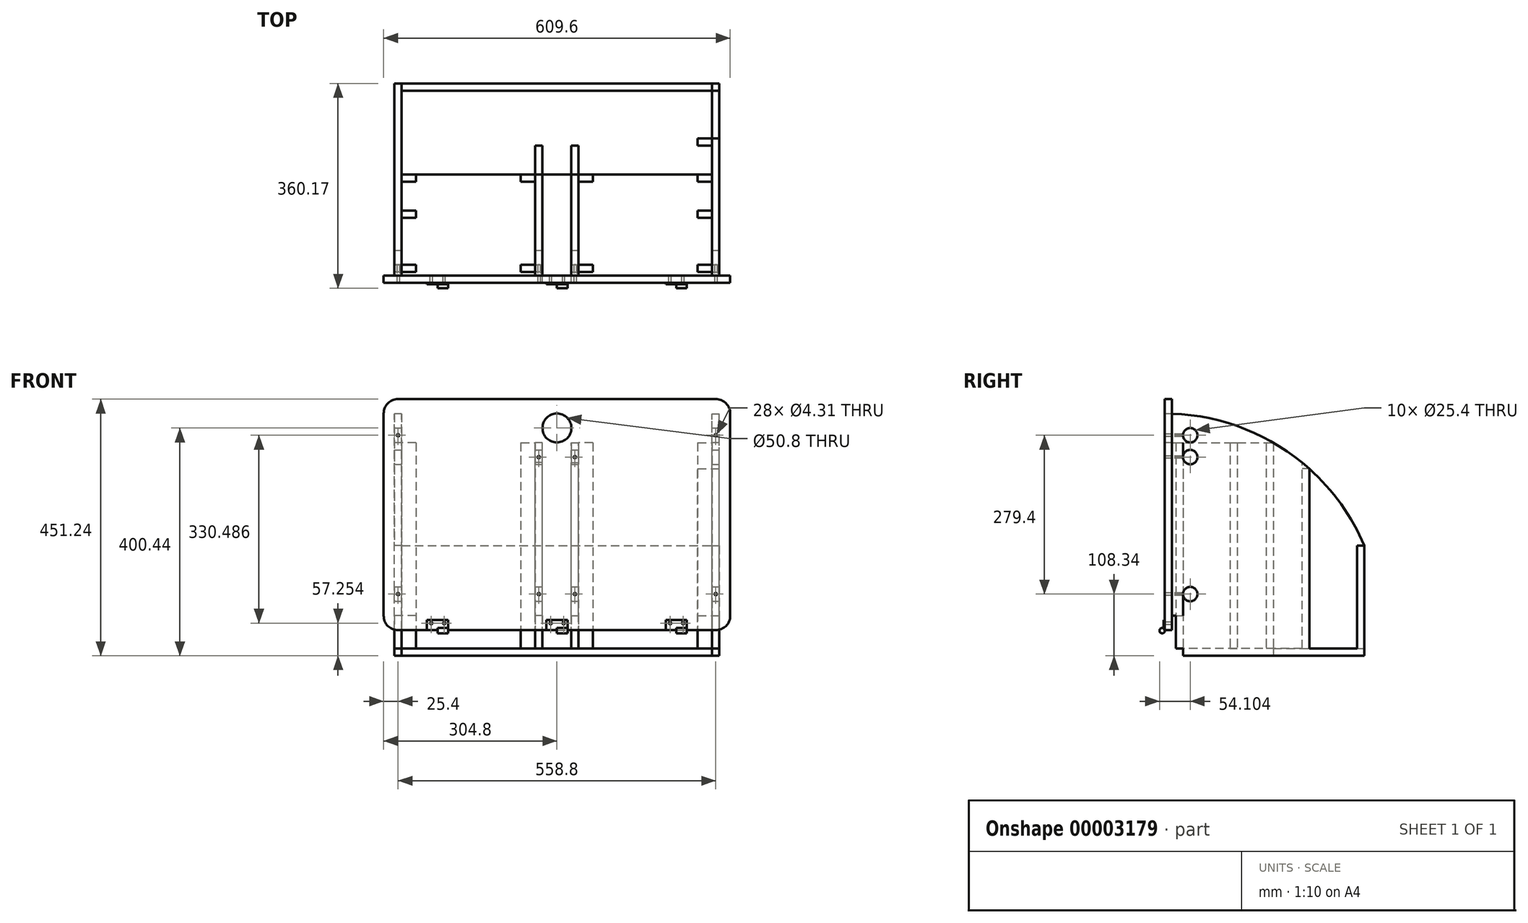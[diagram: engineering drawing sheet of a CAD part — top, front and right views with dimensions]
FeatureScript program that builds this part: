
annotation { "Feature Type Name" : "Feature", "Feature Type Description" : "" }
export const myFeature = defineFeature(function(context is Context, id is Id, definition is map)
    precondition{}
    {
        {
            var Q0;
            Q0=qCreatedBy(makeId("Front.planeOp"),FACE);
            var sketch = newSketch(context, id + "F0", { "sketchPlane" : qUnion([Q0])});
            skLineSegment(sketch, "E0.bottom", {"start": v(25.4, 0) * mm, "end": v(584.2, 0) * mm});
            skLineSegment(sketch, "E0.top", {"start": v(25.4, 406.4) * mm, "end": v(584.2, 406.4) * mm});
            skLineSegment(sketch, "E0.left", {"start": v(0, 25.4) * mm, "end": v(0, 381) * mm});
            skLineSegment(sketch, "E0.right", {"start": v(609.6, 25.4) * mm, "end": v(609.6, 381) * mm});
            skPoint(sketch, "E1.visualSharp", {"position": v(0, 406.4) * mm});
            skArc(sketch, "E1.filletArc", {"start": v(25.4, 406.4) * mm, "mid": v(7.44, 398.96) * mm, "end": v(0, 381) * mm});
            skPoint(sketch, "E2.visualSharp", {"position": v(609.6, 406.4) * mm});
            skArc(sketch, "E2.filletArc", {"start": v(609.6, 381) * mm, "mid": v(602.16, 398.96) * mm, "end": v(584.2, 406.4) * mm});
            skPoint(sketch, "E3.visualSharp", {"position": v(609.6, 0) * mm});
            skArc(sketch, "E3.filletArc", {"start": v(584.2, 0) * mm, "mid": v(602.16, 7.44) * mm, "end": v(609.6, 25.4) * mm});
            skPoint(sketch, "E4.visualSharp", {"position": v(0, 0) * mm});
            skArc(sketch, "E4.filletArc", {"start": v(0, 25.4) * mm, "mid": v(7.44, 7.44) * mm, "end": v(25.4, 0) * mm});
            skCircle(sketch, "E5", {"center": v(304.8, 355.6) * mm, "radius": 25.4 * mm});
            skLineSegment(sketch, "E6.top", {"start": v(76.2, 18.26) * mm, "end": v(113.28, 18.26) * mm});
            skLineSegment(sketch, "E6.left", {"start": v(76.2, -0.8) * mm, "end": v(76.2, 18.26) * mm});
            skLineSegment(sketch, "E6.right", {"start": v(113.28, -0.8) * mm, "end": v(113.28, 18.26) * mm});
            skCircle(sketch, "E7", {"center": v(83.7, 12.41) * mm, "radius": 2.15 * mm});
            skCircle(sketch, "E8", {"center": v(106.55, 12.41) * mm, "radius": 2.15 * mm});
            skLineSegment(sketch, "E9", {"start": v(76.2, -0.8) * mm, "end": v(113.28, -0.8) * mm});
            skLineSegment(sketch, "E10.bottom", {"start": v(286.26, 18.26) * mm, "end": v(323.34, 18.26) * mm});
            skLineSegment(sketch, "E10.top", {"start": v(286.26, -0.8) * mm, "end": v(323.34, -0.8) * mm});
            skLineSegment(sketch, "E10.left", {"start": v(286.26, 18.26) * mm, "end": v(286.26, -0.8) * mm});
            skLineSegment(sketch, "E10.right", {"start": v(323.34, 18.26) * mm, "end": v(323.34, -0.8) * mm});
            skLineSegment(sketch, "E11.bottom", {"start": v(496.32, 18.26) * mm, "end": v(533.4, 18.26) * mm});
            skLineSegment(sketch, "E11.top", {"start": v(496.32, -0.8) * mm, "end": v(533.4, -0.8) * mm});
            skLineSegment(sketch, "E11.left", {"start": v(496.32, 18.26) * mm, "end": v(496.32, -0.8) * mm});
            skLineSegment(sketch, "E11.right", {"start": v(533.4, 18.26) * mm, "end": v(533.4, -0.8) * mm});
            skCircle(sketch, "E12", {"center": v(293.75, 12.41) * mm, "radius": 2.15 * mm});
            skCircle(sketch, "E13", {"center": v(316.61, 12.41) * mm, "radius": 2.15 * mm});
            skCircle(sketch, "E14", {"center": v(503.8, 12.41) * mm, "radius": 2.15 * mm});
            skCircle(sketch, "E15", {"center": v(526.67, 12.41) * mm, "radius": 2.15 * mm});
            skLineSegment(sketch, "E16.bottom", {"start": v(76.2, 3.97) * mm, "end": v(94.87, 3.97) * mm});
            skLineSegment(sketch, "E16.top", {"start": v(76.2, -0.8) * mm, "end": v(94.87, -0.8) * mm});
            skLineSegment(sketch, "E16.left", {"start": v(76.2, 3.97) * mm, "end": v(76.2, -0.8) * mm});
            skLineSegment(sketch, "E16.right", {"start": v(94.87, 3.97) * mm, "end": v(94.87, -0.8) * mm});
            skLineSegment(sketch, "E17.bottom", {"start": v(286.26, 3.97) * mm, "end": v(304.8, 3.97) * mm});
            skLineSegment(sketch, "E17.top", {"start": v(286.26, -0.8) * mm, "end": v(304.8, -0.8) * mm});
            skLineSegment(sketch, "E17.left", {"start": v(286.26, 3.97) * mm, "end": v(286.26, -0.8) * mm});
            skLineSegment(sketch, "E17.right", {"start": v(304.8, 3.97) * mm, "end": v(304.8, -0.8) * mm});
            skLineSegment(sketch, "E18.bottom", {"start": v(496.32, 3.97) * mm, "end": v(514.86, 3.97) * mm});
            skLineSegment(sketch, "E18.top", {"start": v(496.32, -0.8) * mm, "end": v(514.86, -0.8) * mm});
            skLineSegment(sketch, "E18.left", {"start": v(496.32, 3.97) * mm, "end": v(496.32, -0.8) * mm});
            skLineSegment(sketch, "E18.right", {"start": v(514.86, 3.97) * mm, "end": v(514.86, -0.8) * mm});
            skSolve(sketch);
        }
        {
            var Q0;
            Q0=makeQuery(id+"F0.imprint","IMPRINT",FACE,{"disambiguationData":[TD([[makeQuery(id+"F0.imprint","IMPRINT",EDGE,{"derivedFrom":sQuery(id+"F0.wireOp",EDGE,"E0.top")}),-1.0]])]});
            var Q1;
            {var subQ6=sQuery(id+"F0.wireOp",EDGE,"E6.top");Q1=makeQuery(id+"F0.imprint","IMPRINT",FACE,{"disambiguationData":[TD([[makeQuery(id+"F0.imprint","IMPRINT",EDGE,{"derivedFrom":subQ6}),-1.0]])]});}
            var Q2;
            {var subQ6=sQuery(id+"F0.wireOp",EDGE,"E10.bottom");Q2=makeQuery(id+"F0.imprint","IMPRINT",FACE,{"disambiguationData":[TD([[makeQuery(id+"F0.imprint","IMPRINT",EDGE,{"derivedFrom":subQ6}),-1.0]])]});}
            var Q3;
            {var subQ6=sQuery(id+"F0.wireOp",EDGE,"E11.bottom");Q3=makeQuery(id+"F0.imprint","IMPRINT",FACE,{"disambiguationData":[TD([[makeQuery(id+"F0.imprint","IMPRINT",EDGE,{"derivedFrom":subQ6}),-1.0]])]});}
            var Q4;
            {var subQ3=sQuery(id+"F0.wireOp",EDGE,"E16.bottom");Q4=makeQuery(id+"F0.imprint","IMPRINT",FACE,{"disambiguationData":[TD([[makeQuery(id+"F0.imprint","IMPRINT",EDGE,{"derivedFrom":subQ3}),-1.0]])]});}
            var Q5;
            {var subQ3=sQuery(id+"F0.wireOp",EDGE,"E17.bottom");Q5=makeQuery(id+"F0.imprint","IMPRINT",FACE,{"disambiguationData":[TD([[makeQuery(id+"F0.imprint","IMPRINT",EDGE,{"derivedFrom":subQ3}),-1.0]])]});}
            var Q6;
            {var subQ3=sQuery(id+"F0.wireOp",EDGE,"E18.bottom");Q6=makeQuery(id+"F0.imprint","IMPRINT",FACE,{"disambiguationData":[TD([[makeQuery(id+"F0.imprint","IMPRINT",EDGE,{"derivedFrom":subQ3}),-1.0]])]});}
            extrude(context, id + "F1", {"entities" : qUnion([Q0, Q1, Q2, Q3, Q4, Q5, Q6]), "depth" : 12.7 * mm});
        }
        {
            var Q0;
            Q0=makeQuery(id+"F1.opExtrude","SWEPT_FACE",FACE,{"disambiguationData":[OSD([sQuery(id+"F0.wireOp",EDGE,"E0.right")])]});
            cPlane(context, id + "F2", {"entities" : qUnion([Q0]), "cplaneType" : CPlaneType.OFFSET, "offset" : 19.05 * mm, "oppositeDirection" : true, "width" : 152.4 * mm, "height" : 152.4 * mm});
        }
        {
            var Q0;
            Q0=qCreatedBy(id+"F2.planeOp",FACE);
            var sketch = newSketch(context, id + "F3", { "sketchPlane" : qUnion([Q0])});
            skLineSegment(sketch, "E19", {"start": v(0, 0) * mm, "end": v(0, 329.8) * mm});
            skLineSegment(sketch, "E20", {"start": v(0, 329.8) * mm, "end": v(178.05, 329.8) * mm});
            skLineSegment(sketch, "E21.bottom", {"start": v(178.05, 329.8) * mm, "end": v(6.6, 329.8) * mm});
            skLineSegment(sketch, "E21.top", {"start": v(178.05, -32.14) * mm, "end": v(6.6, -32.14) * mm});
            skLineSegment(sketch, "E21.left", {"start": v(178.05, 329.8) * mm, "end": v(178.05, -32.14) * mm});
            skLineSegment(sketch, "E21.right", {"start": v(6.6, 329.8) * mm, "end": v(6.6, -32.14) * mm});
            skLineSegment(sketch, "E22", {"start": v(19.3, 329.8) * mm, "end": v(19.3, -32.14) * mm});
            skLineSegment(sketch, "E23.bottom", {"start": v(101.85, 329.8) * mm, "end": v(114.55, 329.8) * mm});
            skLineSegment(sketch, "E23.top", {"start": v(101.85, -32.14) * mm, "end": v(114.55, -32.14) * mm});
            skLineSegment(sketch, "E23.left", {"start": v(101.85, 329.8) * mm, "end": v(101.85, -32.14) * mm});
            skLineSegment(sketch, "E23.right", {"start": v(114.55, 329.8) * mm, "end": v(114.55, -32.14) * mm});
            skLineSegment(sketch, "E24", {"start": v(165.35, 329.8) * mm, "end": v(165.35, -32.14) * mm});
            skLineSegment(sketch, "E25.bottom", {"start": v(6.6, -32.14) * mm, "end": v(178.05, -32.14) * mm});
            skLineSegment(sketch, "E25.top", {"start": v(6.6, -44.84) * mm, "end": v(178.05, -44.84) * mm});
            skLineSegment(sketch, "E25.left", {"start": v(6.6, -32.14) * mm, "end": v(6.6, -44.84) * mm});
            skLineSegment(sketch, "E25.right", {"start": v(178.05, -32.14) * mm, "end": v(178.05, -44.84) * mm});
            skLineSegment(sketch, "E26", {"start": v(178.05, -44.84) * mm, "end": v(241.55, -44.84) * mm});
            skLineSegment(sketch, "E27", {"start": v(241.55, -44.84) * mm, "end": v(241.55, 283.75) * mm});
            skLineSegment(sketch, "E28.trimOffspring", {"start": v(0, 406.2) * mm, "end": v(0, 406.4) * mm});
            skLineSegment(sketch, "E29", {"start": v(0, 25.4) * mm, "end": v(19.3, 25.4) * mm});
            skLineSegment(sketch, "E30", {"start": v(0, 25.4) * mm, "end": v(0, 381) * mm});
            skLineSegment(sketch, "E31", {"start": v(19.3, -32.14) * mm, "end": v(19.3, -44.84) * mm});
            skLineSegment(sketch, "E32", {"start": v(178.05, -32.14) * mm, "end": v(241.55, -32.14) * mm});
            skLineSegment(sketch, "E33", {"start": v(228.85, -32.14) * mm, "end": v(228.85, 283.75) * mm});
            skLineSegment(sketch, "E34", {"start": v(241.55, 283.75) * mm, "end": v(241.55, 283.75) * mm});
            skLineSegment(sketch, "E35", {"start": v(241.55, 283.75) * mm, "end": v(228.85, 283.75) * mm});
            skLineSegment(sketch, "E36", {"start": v(241.55, -44.84) * mm, "end": v(338.07, -44.84) * mm});
            skLineSegment(sketch, "E37", {"start": v(338.07, -44.84) * mm, "end": v(338.07, 148.74) * mm});
            skCircle(sketch, "E38", {"center": v(-12.7, 0) * mm, "radius": 381 * mm});
            skLineSegment(sketch, "E39", {"start": v(-12.7, 0) * mm, "end": v(-12.7, 381) * mm});
            skLineSegment(sketch, "E40", {"start": v(228.85, 283.75) * mm, "end": v(228.85, 294.64) * mm});
            skLineSegment(sketch, "E41", {"start": v(241.55, -32.14) * mm, "end": v(338.07, -32.14) * mm});
            skLineSegment(sketch, "E42.bottom", {"start": v(338.07, 148.74) * mm, "end": v(325.37, 148.74) * mm});
            skLineSegment(sketch, "E42.top", {"start": v(338.07, -32.14) * mm, "end": v(325.37, -32.14) * mm});
            skLineSegment(sketch, "E42.left", {"start": v(338.07, 148.74) * mm, "end": v(338.07, -32.14) * mm});
            skLineSegment(sketch, "E42.right", {"start": v(325.37, 148.74) * mm, "end": v(325.37, -32.14) * mm});
            skSolve(sketch);
        }
        {
            var Q0;
            {var subQ1=sQuery(id+"F3.wireOp",EDGE,"E20");Q0=makeQuery(id+"F3.imprint","IMPRINT",FACE,{"disambiguationData":[TD([[makeQuery(id+"F3.imprint","IMPRINT",EDGE,{"derivedFrom":subQ1}),-1.0]])]});}
            var Q1;
            {var subQ0=sQuery(id+"F3.wireOp",EDGE,"E22");var subQ3=sQuery(id+"F3.wireOp",EDGE,"E21.bottom");var subQ4=makeQuery(id+"F3.imprint","INTERSECT",VERTEX,{"derivedFrom":[subQ3,subQ0]});Q1=makeQuery(id+"F3.imprint","IMPRINT",FACE,{"disambiguationData":[TD([[makeQuery(id+"F3.imprint","IMPRINT",EDGE,{"disambiguationData":[TD([[subQ4,-1.0]])],"derivedFrom":subQ0}),-1.0]])]});}
            var Q2;
            {var subQ1=sQuery(id+"F3.wireOp",EDGE,"E23.left");Q2=makeQuery(id+"F3.imprint","IMPRINT",FACE,{"disambiguationData":[TD([[makeQuery(id+"F3.imprint","IMPRINT",EDGE,{"derivedFrom":subQ1}),-1.0]])]});}
            var Q3;
            {var subQ1=sQuery(id+"F3.wireOp",EDGE,"E25.right");Q3=makeQuery(id+"F3.imprint","IMPRINT",FACE,{"disambiguationData":[TD([[makeQuery(id+"F3.imprint","IMPRINT",EDGE,{"derivedFrom":subQ1}),-1.0]])]});}
            var Q4;
            Q4=makeQuery(id+"F3.imprint","IMPRINT",FACE,{"disambiguationData":[TD([[makeQuery(id+"F3.imprint","IMPRINT",EDGE,{"derivedFrom":sQuery(id+"F3.wireOp",EDGE,"E23.bottom")}),-1.0]])]});
            var Q5;
            {var subQ2=sQuery(id+"F3.wireOp",EDGE,"E23.right");Q5=makeQuery(id+"F3.imprint","IMPRINT",FACE,{"disambiguationData":[TD([[makeQuery(id+"F3.imprint","IMPRINT",EDGE,{"derivedFrom":subQ2}),1.0]])]});}
            var Q6;
            {var subQ1=sQuery(id+"F3.wireOp",EDGE,"E21.left");Q6=makeQuery(id+"F3.imprint","IMPRINT",FACE,{"disambiguationData":[TD([[makeQuery(id+"F3.imprint","IMPRINT",EDGE,{"derivedFrom":subQ1}),-1.0]])]});}
            var Q7;
            {var subQ3=sQuery(id+"F3.wireOp",EDGE,"E20");Q7=makeQuery(id+"F3.imprint","IMPRINT",FACE,{"disambiguationData":[TD([[makeQuery(id+"F3.imprint","IMPRINT",EDGE,{"derivedFrom":subQ3}),1.0]])]});}
            var Q8;
            {var subQ1=sQuery(id+"F3.wireOp",EDGE,"E21.left");Q8=makeQuery(id+"F3.imprint","IMPRINT",FACE,{"disambiguationData":[TD([[makeQuery(id+"F3.imprint","IMPRINT",EDGE,{"derivedFrom":subQ1}),1.0]])]});}
            var Q9;
            {var subQ1=sQuery(id+"F3.wireOp",EDGE,"E33");Q9=makeQuery(id+"F3.imprint","IMPRINT",FACE,{"disambiguationData":[TD([[makeQuery(id+"F3.imprint","IMPRINT",EDGE,{"derivedFrom":subQ1}),-1.0]])]});}
            var Q10;
            {var subQ4=sQuery(id+"F3.wireOp",EDGE,"E25.right");Q10=makeQuery(id+"F3.imprint","IMPRINT",FACE,{"disambiguationData":[TD([[makeQuery(id+"F3.imprint","IMPRINT",EDGE,{"derivedFrom":subQ4}),1.0]])]});}
            var Q11;
            {var subQ4=sQuery(id+"F3.wireOp",EDGE,"E36");Q11=makeQuery(id+"F3.imprint","IMPRINT",FACE,{"disambiguationData":[TD([[makeQuery(id+"F3.imprint","IMPRINT",EDGE,{"derivedFrom":subQ4}),1.0]])]});}
            var Q12;
            {var subQ2=sQuery(id+"F3.wireOp",EDGE,"E35");Q12=makeQuery(id+"F3.imprint","IMPRINT",FACE,{"disambiguationData":[TD([[makeQuery(id+"F3.imprint","IMPRINT",EDGE,{"derivedFrom":subQ2}),-1.0]])]});}
            var Q13;
            {var subQ0=sQuery(id+"F3.wireOp",EDGE,"E41");Q13=makeQuery(id+"F3.imprint","IMPRINT",FACE,{"disambiguationData":[TD([[makeQuery(id+"F3.imprint","IMPRINT",EDGE,{"derivedFrom":subQ0}),1.0]])]});}
            var Q14;
            Q14=makeQuery(id+"F3.imprint","IMPRINT",FACE,{"disambiguationData":[TD([[makeQuery(id+"F3.imprint","IMPRINT",EDGE,{"derivedFrom":sQuery(id+"F3.wireOp",EDGE,"E42.bottom")}),1.0]])]});
            extrude(context, id + "F4", {"entities" : qUnion([Q0, Q1, Q2, Q3, Q4, Q5, Q6, Q7, Q8, Q9, Q10, Q11, Q12, Q13, Q14]), "oppositeDirection" : true, "depth" : 12.7 * mm});
        }
        {
            var Q0;
            Q0=makeQuery(id+"F1.opExtrude","SWEPT_FACE",FACE,{"disambiguationData":[OSD([sQuery(id+"F0.wireOp",EDGE,"E0.left")])]});
            cPlane(context, id + "F5", {"entities" : qUnion([Q0]), "cplaneType" : CPlaneType.OFFSET, "offset" : 19.05 * mm, "oppositeDirection" : true, "width" : 152.4 * mm, "height" : 152.4 * mm});
        }
        {
            var Q0;
            Q0=qCreatedBy(id+"F5.planeOp",FACE);
            var sketch = newSketch(context, id + "F6", { "sketchPlane" : qUnion([Q0])});
            skLineSegment(sketch, "E43.0", {"start": v(0, 0) * mm, "end": v(0, 329.8) * mm});
            skLineSegment(sketch, "E43.1", {"start": v(0, 329.8) * mm, "end": v(-178.05, 329.8) * mm});
            skLineSegment(sketch, "E43.2", {"start": v(-178.05, 329.8) * mm, "end": v(-6.6, 329.8) * mm});
            skLineSegment(sketch, "E43.3", {"start": v(-178.05, -32.14) * mm, "end": v(-6.6, -32.14) * mm});
            skLineSegment(sketch, "E43.4", {"start": v(-178.05, 329.8) * mm, "end": v(-178.05, -32.14) * mm});
            skLineSegment(sketch, "E43.5", {"start": v(-6.6, 329.8) * mm, "end": v(-6.6, -32.14) * mm});
            skLineSegment(sketch, "E43.6", {"start": v(-19.3, 329.8) * mm, "end": v(-19.3, -32.14) * mm});
            skLineSegment(sketch, "E43.7", {"start": v(-101.85, 329.8) * mm, "end": v(-114.55, 329.8) * mm});
            skLineSegment(sketch, "E43.8", {"start": v(-101.85, -32.14) * mm, "end": v(-114.55, -32.14) * mm});
            skLineSegment(sketch, "E43.9", {"start": v(-101.85, 329.8) * mm, "end": v(-101.85, -32.14) * mm});
            skLineSegment(sketch, "E43.10", {"start": v(-114.55, 329.8) * mm, "end": v(-114.55, -32.14) * mm});
            skLineSegment(sketch, "E43.11", {"start": v(-165.35, 329.8) * mm, "end": v(-165.35, -32.14) * mm});
            skLineSegment(sketch, "E43.12", {"start": v(-6.6, -32.14) * mm, "end": v(-178.05, -32.14) * mm});
            skLineSegment(sketch, "E43.13", {"start": v(-6.6, -44.84) * mm, "end": v(-178.05, -44.84) * mm});
            skLineSegment(sketch, "E43.14", {"start": v(-6.6, -32.14) * mm, "end": v(-6.6, -44.84) * mm});
            skLineSegment(sketch, "E43.15", {"start": v(-178.05, -32.14) * mm, "end": v(-178.05, -44.84) * mm});
            skLineSegment(sketch, "E43.16", {"start": v(-178.05, -44.84) * mm, "end": v(-241.55, -44.84) * mm});
            skLineSegment(sketch, "E43.17", {"start": v(-241.55, -44.84) * mm, "end": v(-241.55, 283.75) * mm});
            skLineSegment(sketch, "E43.18", {"start": v(0, 406.2) * mm, "end": v(0, 406.4) * mm});
            skLineSegment(sketch, "E43.19", {"start": v(0, 25.4) * mm, "end": v(-19.3, 25.4) * mm});
            skLineSegment(sketch, "E43.20", {"start": v(0, 25.4) * mm, "end": v(0, 381) * mm});
            skLineSegment(sketch, "E43.21", {"start": v(-19.3, -32.14) * mm, "end": v(-19.3, -44.84) * mm});
            skLineSegment(sketch, "E43.22", {"start": v(-178.05, -32.14) * mm, "end": v(-241.55, -32.14) * mm});
            skLineSegment(sketch, "E43.23", {"start": v(-228.85, -32.14) * mm, "end": v(-228.85, 283.75) * mm});
            skPoint(sketch, "E43.24", {"position": v(-241.55, 283.75) * mm});
            skLineSegment(sketch, "E43.25", {"start": v(-241.55, 283.75) * mm, "end": v(-228.85, 283.75) * mm});
            skLineSegment(sketch, "E43.26", {"start": v(-241.55, -44.84) * mm, "end": v(-338.07, -44.84) * mm});
            skLineSegment(sketch, "E43.27", {"start": v(-338.07, -44.84) * mm, "end": v(-338.07, 148.74) * mm});
            skCircle(sketch, "E43.28", {"center": v(12.7, 0) * mm, "radius": 381 * mm});
            skLineSegment(sketch, "E43.29", {"start": v(12.7, 0) * mm, "end": v(12.7, 381) * mm});
            skLineSegment(sketch, "E44.0", {"start": v(-228.85, 283.75) * mm, "end": v(-228.85, 294.64) * mm});
            skSolve(sketch);
        }
        {
            var Q0;
            {var subQ4=sQuery(id+"F6.wireOp",EDGE,"E43.26");Q0=makeQuery(id+"F6.imprint","IMPRINT",FACE,{"disambiguationData":[TD([[makeQuery(id+"F6.imprint","IMPRINT",EDGE,{"derivedFrom":subQ4}),-1.0]])]});}
            var Q1;
            {var subQ1=sQuery(id+"F6.wireOp",EDGE,"E43.23");Q1=makeQuery(id+"F6.imprint","IMPRINT",FACE,{"disambiguationData":[TD([[makeQuery(id+"F6.imprint","IMPRINT",EDGE,{"derivedFrom":subQ1}),1.0]])]});}
            var Q2;
            {var subQ2=sQuery(id+"F6.wireOp",EDGE,"E43.4");Q2=makeQuery(id+"F6.imprint","IMPRINT",FACE,{"disambiguationData":[TD([[makeQuery(id+"F6.imprint","IMPRINT",EDGE,{"derivedFrom":subQ2}),-1.0]])]});}
            var Q3;
            {var subQ2=sQuery(id+"F6.wireOp",EDGE,"E43.15");Q3=makeQuery(id+"F6.imprint","IMPRINT",FACE,{"disambiguationData":[TD([[makeQuery(id+"F6.imprint","IMPRINT",EDGE,{"derivedFrom":subQ2}),1.0]])]});}
            var Q4;
            {var subQ4=sQuery(id+"F6.wireOp",EDGE,"E43.15");Q4=makeQuery(id+"F6.imprint","IMPRINT",FACE,{"disambiguationData":[TD([[makeQuery(id+"F6.imprint","IMPRINT",EDGE,{"derivedFrom":subQ4}),-1.0]])]});}
            var Q5;
            {var subQ1=sQuery(id+"F6.wireOp",EDGE,"E43.4");Q5=makeQuery(id+"F6.imprint","IMPRINT",FACE,{"disambiguationData":[TD([[makeQuery(id+"F6.imprint","IMPRINT",EDGE,{"derivedFrom":subQ1}),1.0]])]});}
            var Q6;
            {var subQ2=sQuery(id+"F6.wireOp",EDGE,"E43.10");Q6=makeQuery(id+"F6.imprint","IMPRINT",FACE,{"disambiguationData":[TD([[makeQuery(id+"F6.imprint","IMPRINT",EDGE,{"derivedFrom":subQ2}),-1.0]])]});}
            var Q7;
            {var subQ5=sQuery(id+"F6.wireOp",EDGE,"E43.1");Q7=makeQuery(id+"F6.imprint","IMPRINT",FACE,{"disambiguationData":[TD([[makeQuery(id+"F6.imprint","IMPRINT",EDGE,{"derivedFrom":subQ5}),-1.0]])]});}
            var Q8;
            Q8=makeQuery(id+"F6.imprint","IMPRINT",FACE,{"disambiguationData":[TD([[makeQuery(id+"F6.imprint","IMPRINT",EDGE,{"derivedFrom":sQuery(id+"F6.wireOp",EDGE,"E43.7")}),1.0]])]});
            var Q9;
            {var subQ1=sQuery(id+"F6.wireOp",EDGE,"E43.9");Q9=makeQuery(id+"F6.imprint","IMPRINT",FACE,{"disambiguationData":[TD([[makeQuery(id+"F6.imprint","IMPRINT",EDGE,{"derivedFrom":subQ1}),1.0]])]});}
            var Q10;
            {var subQ0=sQuery(id+"F6.wireOp",EDGE,"E43.6");var subQ3=sQuery(id+"F6.wireOp",EDGE,"E43.2");var subQ4=makeQuery(id+"F6.imprint","INTERSECT",VERTEX,{"derivedFrom":[subQ3,subQ0]});Q10=makeQuery(id+"F6.imprint","IMPRINT",FACE,{"disambiguationData":[TD([[makeQuery(id+"F6.imprint","IMPRINT",EDGE,{"disambiguationData":[TD([[subQ4,-1.0]])],"derivedFrom":subQ0}),1.0]])]});}
            var Q11;
            {var subQ1=sQuery(id+"F6.wireOp",EDGE,"E43.1");Q11=makeQuery(id+"F6.imprint","IMPRINT",FACE,{"disambiguationData":[TD([[makeQuery(id+"F6.imprint","IMPRINT",EDGE,{"derivedFrom":subQ1}),1.0]])]});}
            var Q12;
            {var subQ2=sQuery(id+"F6.wireOp",EDGE,"E43.25");Q12=makeQuery(id+"F6.imprint","IMPRINT",FACE,{"disambiguationData":[TD([[makeQuery(id+"F6.imprint","IMPRINT",EDGE,{"derivedFrom":subQ2}),1.0]])]});}
            extrude(context, id + "F7", {"entities" : qUnion([Q0, Q1, Q2, Q3, Q4, Q5, Q6, Q7, Q8, Q9, Q10, Q11, Q12]), "oppositeDirection" : true, "depth" : 12.7 * mm});
        }
        {
            var Q0;
            Q0=makeQuery(id+"F4.opExtrude","CAP_FACE",FACE,{"disambiguationData":[OSD([sQuery(id+"F3.wireOp",EDGE,"E22"),sQuery(id+"F3.wireOp",EDGE,"E25.top"),sQuery(id+"F3.wireOp",EDGE,"E26"),sQuery(id+"F3.wireOp",EDGE,"E29"),sQuery(id+"F3.wireOp",EDGE,"E30"),sQuery(id+"F3.wireOp",EDGE,"E31"),sQuery(id+"F3.wireOp",EDGE,"E36"),sQuery(id+"F3.wireOp",EDGE,"E37"),sQuery(id+"F3.wireOp",EDGE,"E38"),sQuery(id+"F3.wireOp",EDGE,"E42.left")])],"isStart":false});
            cPlane(context, id + "F8", {"entities" : qUnion([Q0]), "cplaneType" : CPlaneType.OFFSET, "offset" : 234.95 * mm, "width" : 152.4 * mm, "height" : 152.4 * mm});
        }
        {
            var Q0;
            Q0=qCreatedBy(id+"F8.planeOp",FACE);
            var sketch = newSketch(context, id + "F9", { "sketchPlane" : qUnion([Q0])});
            skLineSegment(sketch, "E45.0", {"start": v(0, 0) * mm, "end": v(0, 329.8) * mm});
            skLineSegment(sketch, "E45.1", {"start": v(0, 329.8) * mm, "end": v(-178.05, 329.8) * mm});
            skLineSegment(sketch, "E45.2", {"start": v(-178.05, 329.8) * mm, "end": v(-6.6, 329.8) * mm});
            skLineSegment(sketch, "E45.3", {"start": v(-178.05, -32.14) * mm, "end": v(-6.6, -32.14) * mm});
            skLineSegment(sketch, "E45.4", {"start": v(-178.05, 329.8) * mm, "end": v(-178.05, -32.14) * mm});
            skLineSegment(sketch, "E45.5", {"start": v(-6.6, 329.8) * mm, "end": v(-6.6, -32.14) * mm});
            skLineSegment(sketch, "E45.6", {"start": v(-19.3, 329.8) * mm, "end": v(-19.3, -32.14) * mm});
            skLineSegment(sketch, "E45.7", {"start": v(-101.85, 329.8) * mm, "end": v(-114.55, 329.8) * mm});
            skLineSegment(sketch, "E45.8", {"start": v(-101.85, -32.14) * mm, "end": v(-114.55, -32.14) * mm});
            skLineSegment(sketch, "E45.9", {"start": v(-101.85, 329.8) * mm, "end": v(-101.85, -32.14) * mm});
            skLineSegment(sketch, "E45.10", {"start": v(-114.55, 329.8) * mm, "end": v(-114.55, -32.14) * mm});
            skLineSegment(sketch, "E45.11", {"start": v(-165.35, 329.8) * mm, "end": v(-165.35, -32.14) * mm});
            skLineSegment(sketch, "E45.12", {"start": v(-6.6, -32.14) * mm, "end": v(-178.05, -32.14) * mm});
            skLineSegment(sketch, "E45.13", {"start": v(-6.6, -44.84) * mm, "end": v(-178.05, -44.84) * mm});
            skLineSegment(sketch, "E45.14", {"start": v(-6.6, -32.14) * mm, "end": v(-6.6, -44.84) * mm});
            skLineSegment(sketch, "E45.15", {"start": v(-178.05, -32.14) * mm, "end": v(-178.05, -44.84) * mm});
            skLineSegment(sketch, "E45.16", {"start": v(-178.05, -44.84) * mm, "end": v(-241.55, -44.84) * mm});
            skLineSegment(sketch, "E45.17", {"start": v(-241.55, -44.84) * mm, "end": v(-241.55, 283.75) * mm});
            skLineSegment(sketch, "E45.18", {"start": v(0, 406.2) * mm, "end": v(0, 406.4) * mm});
            skLineSegment(sketch, "E45.19", {"start": v(0, 25.4) * mm, "end": v(-19.3, 25.4) * mm});
            skLineSegment(sketch, "E45.20", {"start": v(0, 25.4) * mm, "end": v(0, 381) * mm});
            skLineSegment(sketch, "E45.21", {"start": v(-19.3, -32.14) * mm, "end": v(-19.3, -44.84) * mm});
            skLineSegment(sketch, "E45.22", {"start": v(-178.05, -32.14) * mm, "end": v(-241.55, -32.14) * mm});
            skLineSegment(sketch, "E45.23", {"start": v(-228.85, -32.14) * mm, "end": v(-228.85, 283.75) * mm});
            skPoint(sketch, "E45.24", {"position": v(-241.55, 283.75) * mm});
            skLineSegment(sketch, "E45.25", {"start": v(-241.55, 283.75) * mm, "end": v(-228.85, 283.75) * mm});
            skLineSegment(sketch, "E45.26", {"start": v(-241.55, -44.84) * mm, "end": v(-338.07, -44.84) * mm});
            skLineSegment(sketch, "E45.27", {"start": v(-338.07, -44.84) * mm, "end": v(-338.07, 148.74) * mm});
            skCircle(sketch, "E45.28", {"center": v(12.7, 0) * mm, "radius": 381 * mm});
            skLineSegment(sketch, "E45.29", {"start": v(12.7, 0) * mm, "end": v(12.7, 381) * mm});
            skLineSegment(sketch, "E46.0", {"start": v(-228.85, 283.75) * mm, "end": v(-228.85, 294.64) * mm});
            skSolve(sketch);
        }
        {
            var Q0;
            {var subQ1=sQuery(id+"F9.wireOp",EDGE,"E45.9");Q0=makeQuery(id+"F9.imprint","IMPRINT",FACE,{"disambiguationData":[TD([[makeQuery(id+"F9.imprint","IMPRINT",EDGE,{"derivedFrom":subQ1}),1.0]])]});}
            var Q1;
            {var subQ1=sQuery(id+"F9.wireOp",EDGE,"E45.1");Q1=makeQuery(id+"F9.imprint","IMPRINT",FACE,{"disambiguationData":[TD([[makeQuery(id+"F9.imprint","IMPRINT",EDGE,{"derivedFrom":subQ1}),1.0]])]});}
            var Q2;
            {var subQ3=sQuery(id+"F9.wireOp",EDGE,"E45.6");var subQ5=sQuery(id+"F9.wireOp",EDGE,"E45.2");var subQ6=makeQuery(id+"F9.imprint","INTERSECT",VERTEX,{"derivedFrom":[subQ5,subQ3]});Q2=makeQuery(id+"F9.imprint","IMPRINT",FACE,{"disambiguationData":[TD([[makeQuery(id+"F9.imprint","IMPRINT",EDGE,{"disambiguationData":[TD([[subQ6,-1.0]])],"derivedFrom":subQ3}),1.0]])]});}
            var Q3;
            Q3=makeQuery(id+"F9.imprint","IMPRINT",FACE,{"disambiguationData":[TD([[makeQuery(id+"F9.imprint","IMPRINT",EDGE,{"derivedFrom":sQuery(id+"F9.wireOp",EDGE,"E45.7")}),1.0]])]});
            var Q4;
            {var subQ2=sQuery(id+"F9.wireOp",EDGE,"E45.10");Q4=makeQuery(id+"F9.imprint","IMPRINT",FACE,{"disambiguationData":[TD([[makeQuery(id+"F9.imprint","IMPRINT",EDGE,{"derivedFrom":subQ2}),-1.0]])]});}
            var Q5;
            {var subQ2=sQuery(id+"F9.wireOp",EDGE,"E45.4");Q5=makeQuery(id+"F9.imprint","IMPRINT",FACE,{"disambiguationData":[TD([[makeQuery(id+"F9.imprint","IMPRINT",EDGE,{"derivedFrom":subQ2}),1.0]])]});}
            var Q6;
            {var subQ2=sQuery(id+"F9.wireOp",EDGE,"E45.4");Q6=makeQuery(id+"F9.imprint","IMPRINT",FACE,{"disambiguationData":[TD([[makeQuery(id+"F9.imprint","IMPRINT",EDGE,{"derivedFrom":subQ2}),-1.0]])]});}
            extrude(context, id + "F10", {"entities" : qUnion([Q0, Q1, Q2, Q3, Q4, Q5, Q6]), "depth" : 12.7 * mm});
        }
        {
            var Q0;
            Q0=makeQuery(id+"F7.opExtrude","CAP_FACE",FACE,{"disambiguationData":[OSD([sQuery(id+"F6.wireOp",EDGE,"E43.6"),sQuery(id+"F6.wireOp",EDGE,"E43.13"),sQuery(id+"F6.wireOp",EDGE,"E43.16"),sQuery(id+"F6.wireOp",EDGE,"E43.19"),sQuery(id+"F6.wireOp",EDGE,"E43.20"),sQuery(id+"F6.wireOp",EDGE,"E43.21"),sQuery(id+"F6.wireOp",EDGE,"E43.26"),sQuery(id+"F6.wireOp",EDGE,"E43.27"),sQuery(id+"F6.wireOp",EDGE,"E43.28")])],"isStart":false});
            cPlane(context, id + "F11", {"entities" : qUnion([Q0]), "cplaneType" : CPlaneType.OFFSET, "offset" : 234.95 * mm, "width" : 152.4 * mm, "height" : 152.4 * mm});
        }
        {
            var Q0;
            Q0=qCreatedBy(id+"F11.planeOp",FACE);
            var sketch = newSketch(context, id + "F12", { "sketchPlane" : qUnion([Q0])});
            skLineSegment(sketch, "E47.0", {"start": v(0, 0) * mm, "end": v(0, 329.8) * mm});
            skLineSegment(sketch, "E47.1", {"start": v(0, 329.8) * mm, "end": v(178.05, 329.8) * mm});
            skLineSegment(sketch, "E47.2", {"start": v(178.05, 329.8) * mm, "end": v(6.6, 329.8) * mm});
            skLineSegment(sketch, "E47.3", {"start": v(178.05, -32.14) * mm, "end": v(6.6, -32.14) * mm});
            skLineSegment(sketch, "E47.4", {"start": v(178.05, 329.8) * mm, "end": v(178.05, -32.14) * mm});
            skLineSegment(sketch, "E47.5", {"start": v(6.6, 329.8) * mm, "end": v(6.6, -32.14) * mm});
            skLineSegment(sketch, "E47.6", {"start": v(19.3, 329.8) * mm, "end": v(19.3, -32.14) * mm});
            skLineSegment(sketch, "E47.7", {"start": v(101.85, 329.8) * mm, "end": v(114.55, 329.8) * mm});
            skLineSegment(sketch, "E47.8", {"start": v(101.85, -32.14) * mm, "end": v(114.55, -32.14) * mm});
            skLineSegment(sketch, "E47.9", {"start": v(101.85, 329.8) * mm, "end": v(101.85, -32.14) * mm});
            skLineSegment(sketch, "E47.10", {"start": v(114.55, 329.8) * mm, "end": v(114.55, -32.14) * mm});
            skLineSegment(sketch, "E47.11", {"start": v(165.35, 329.8) * mm, "end": v(165.35, -32.14) * mm});
            skLineSegment(sketch, "E47.12", {"start": v(6.6, -32.14) * mm, "end": v(178.05, -32.14) * mm});
            skLineSegment(sketch, "E47.13", {"start": v(6.6, -44.84) * mm, "end": v(178.05, -44.84) * mm});
            skLineSegment(sketch, "E47.14", {"start": v(6.6, -32.14) * mm, "end": v(6.6, -44.84) * mm});
            skLineSegment(sketch, "E47.15", {"start": v(178.05, -32.14) * mm, "end": v(178.05, -44.84) * mm});
            skLineSegment(sketch, "E47.16", {"start": v(178.05, -44.84) * mm, "end": v(241.55, -44.84) * mm});
            skLineSegment(sketch, "E47.17", {"start": v(241.55, -44.84) * mm, "end": v(241.55, 283.75) * mm});
            skLineSegment(sketch, "E47.18", {"start": v(0, 406.2) * mm, "end": v(0, 406.4) * mm});
            skLineSegment(sketch, "E47.19", {"start": v(0, 25.4) * mm, "end": v(19.3, 25.4) * mm});
            skLineSegment(sketch, "E47.20", {"start": v(0, 25.4) * mm, "end": v(0, 381) * mm});
            skLineSegment(sketch, "E47.21", {"start": v(19.3, -32.14) * mm, "end": v(19.3, -44.84) * mm});
            skLineSegment(sketch, "E47.22", {"start": v(178.05, -32.14) * mm, "end": v(241.55, -32.14) * mm});
            skLineSegment(sketch, "E47.23", {"start": v(228.85, -32.14) * mm, "end": v(228.85, 283.75) * mm});
            skPoint(sketch, "E47.24", {"position": v(241.55, 283.75) * mm});
            skLineSegment(sketch, "E47.25", {"start": v(241.55, 283.75) * mm, "end": v(228.85, 283.75) * mm});
            skLineSegment(sketch, "E47.26", {"start": v(241.55, -44.84) * mm, "end": v(338.07, -44.84) * mm});
            skLineSegment(sketch, "E47.27", {"start": v(338.07, -44.84) * mm, "end": v(338.07, 148.74) * mm});
            skCircle(sketch, "E47.28", {"center": v(-12.7, 0) * mm, "radius": 381 * mm});
            skLineSegment(sketch, "E47.29", {"start": v(-12.7, 0) * mm, "end": v(-12.7, 381) * mm});
            skLineSegment(sketch, "E48.0", {"start": v(228.85, 283.75) * mm, "end": v(228.85, 294.64) * mm});
            skSolve(sketch);
        }
        {
            var Q0;
            {var subQ1=sQuery(id+"F12.wireOp",EDGE,"E47.9");Q0=makeQuery(id+"F12.imprint","IMPRINT",FACE,{"disambiguationData":[TD([[makeQuery(id+"F12.imprint","IMPRINT",EDGE,{"derivedFrom":subQ1}),-1.0]])]});}
            var Q1;
            {var subQ1=sQuery(id+"F12.wireOp",EDGE,"E47.1");Q1=makeQuery(id+"F12.imprint","IMPRINT",FACE,{"disambiguationData":[TD([[makeQuery(id+"F12.imprint","IMPRINT",EDGE,{"derivedFrom":subQ1}),-1.0]])]});}
            var Q2;
            {var subQ3=sQuery(id+"F12.wireOp",EDGE,"E47.6");var subQ5=sQuery(id+"F12.wireOp",EDGE,"E47.2");var subQ6=makeQuery(id+"F12.imprint","INTERSECT",VERTEX,{"derivedFrom":[subQ5,subQ3]});Q2=makeQuery(id+"F12.imprint","IMPRINT",FACE,{"disambiguationData":[TD([[makeQuery(id+"F12.imprint","IMPRINT",EDGE,{"disambiguationData":[TD([[subQ6,-1.0]])],"derivedFrom":subQ3}),-1.0]])]});}
            var Q3;
            Q3=makeQuery(id+"F12.imprint","IMPRINT",FACE,{"disambiguationData":[TD([[makeQuery(id+"F12.imprint","IMPRINT",EDGE,{"derivedFrom":sQuery(id+"F12.wireOp",EDGE,"E47.7")}),-1.0]])]});
            var Q4;
            {var subQ2=sQuery(id+"F12.wireOp",EDGE,"E47.10");Q4=makeQuery(id+"F12.imprint","IMPRINT",FACE,{"disambiguationData":[TD([[makeQuery(id+"F12.imprint","IMPRINT",EDGE,{"derivedFrom":subQ2}),1.0]])]});}
            var Q5;
            {var subQ2=sQuery(id+"F12.wireOp",EDGE,"E47.4");Q5=makeQuery(id+"F12.imprint","IMPRINT",FACE,{"disambiguationData":[TD([[makeQuery(id+"F12.imprint","IMPRINT",EDGE,{"derivedFrom":subQ2}),-1.0]])]});}
            var Q6;
            {var subQ2=sQuery(id+"F12.wireOp",EDGE,"E47.4");Q6=makeQuery(id+"F12.imprint","IMPRINT",FACE,{"disambiguationData":[TD([[makeQuery(id+"F12.imprint","IMPRINT",EDGE,{"derivedFrom":subQ2}),1.0]])]});}
            extrude(context, id + "F13", {"entities" : qUnion([Q0, Q1, Q2, Q3, Q4, Q5, Q6]), "depth" : 12.7 * mm});
        }
        {
            var Q0;
            Q0=makeQuery(id+"F4.opExtrude","CAP_FACE",FACE,{"disambiguationData":[OSD([sQuery(id+"F3.wireOp",EDGE,"E22"),sQuery(id+"F3.wireOp",EDGE,"E25.top"),sQuery(id+"F3.wireOp",EDGE,"E26"),sQuery(id+"F3.wireOp",EDGE,"E29"),sQuery(id+"F3.wireOp",EDGE,"E30"),sQuery(id+"F3.wireOp",EDGE,"E31"),sQuery(id+"F3.wireOp",EDGE,"E36"),sQuery(id+"F3.wireOp",EDGE,"E37"),sQuery(id+"F3.wireOp",EDGE,"E38"),sQuery(id+"F3.wireOp",EDGE,"E42.left")])],"isStart":false});
            var sketch = newSketch(context, id + "F14", { "sketchPlane" : qUnion([Q0])});
            skLineSegment(sketch, "E49.0", {"start": v(-19.3, 329.8) * mm, "end": v(-19.3, -32.14) * mm});
            skLineSegment(sketch, "E50.0", {"start": v(0, 329.8) * mm, "end": v(-178.05, 329.8) * mm});
            skLineSegment(sketch, "E51.0", {"start": v(-6.6, 329.8) * mm, "end": v(-6.6, -32.14) * mm});
            skLineSegment(sketch, "E52.0", {"start": v(0, 25.4) * mm, "end": v(-19.3, 25.4) * mm});
            skLineSegment(sketch, "E53.0", {"start": v(-114.55, 329.8) * mm, "end": v(-114.55, -32.14) * mm});
            skLineSegment(sketch, "E54.0", {"start": v(-101.85, 329.8) * mm, "end": v(-101.85, -32.14) * mm});
            skLineSegment(sketch, "E55.0", {"start": v(-101.85, -32.14) * mm, "end": v(-114.55, -32.14) * mm});
            skLineSegment(sketch, "E56.0", {"start": v(-6.6, -32.14) * mm, "end": v(-178.05, -32.14) * mm});
            skLineSegment(sketch, "E57.0", {"start": v(-178.05, 329.8) * mm, "end": v(-178.05, -32.14) * mm});
            skLineSegment(sketch, "E58.0", {"start": v(-165.35, 329.8) * mm, "end": v(-165.35, -32.14) * mm});
            skLineSegment(sketch, "E59.0.0", {"start": v(-228.85, -32.14) * mm, "end": v(-241.55, -32.14) * mm});
            skLineSegment(sketch, "E59.0.1", {"start": v(-241.55, -32.14) * mm, "end": v(-241.55, 283.75) * mm});
            skLineSegment(sketch, "E59.0.2", {"start": v(-241.55, 283.75) * mm, "end": v(-228.85, 283.75) * mm});
            skLineSegment(sketch, "E59.0.3", {"start": v(-228.85, -32.14) * mm, "end": v(-228.85, 283.75) * mm});
            skLineSegment(sketch, "E60.0.0", {"start": v(-178.05, -32.14) * mm, "end": v(-228.85, -32.14) * mm});
            skLineSegment(sketch, "E60.0.1", {"start": v(-178.05, -32.14) * mm, "end": v(-178.05, -44.84) * mm});
            skLineSegment(sketch, "E60.0.2", {"start": v(-178.05, -44.84) * mm, "end": v(-241.55, -44.84) * mm});
            skLineSegment(sketch, "E60.0.3", {"start": v(-241.55, -44.84) * mm, "end": v(-241.55, -32.14) * mm});
            skLineSegment(sketch, "E61.0.0", {"start": v(-19.3, -32.14) * mm, "end": v(-101.85, -32.14) * mm});
            skLineSegment(sketch, "E61.0.1", {"start": v(-19.3, -32.14) * mm, "end": v(-19.3, -44.84) * mm});
            skLineSegment(sketch, "E61.0.2", {"start": v(-19.3, -44.84) * mm, "end": v(-178.05, -44.84) * mm});
            skLineSegment(sketch, "E61.0.4", {"start": v(-165.35, -32.14) * mm, "end": v(-178.05, -32.14) * mm});
            skLineSegment(sketch, "E61.0.5", {"start": v(-114.55, -32.14) * mm, "end": v(-165.35, -32.14) * mm});
            skLineSegment(sketch, "E62.0", {"start": v(-241.55, -44.84) * mm, "end": v(-338.07, -44.84) * mm});
            skLineSegment(sketch, "E62.1", {"start": v(-338.07, -44.84) * mm, "end": v(-338.07, 148.74) * mm});
            skLineSegment(sketch, "E63.0", {"start": v(-241.55, -32.14) * mm, "end": v(-338.07, -32.14) * mm});
            skLineSegment(sketch, "E64.0", {"start": v(-338.07, 148.74) * mm, "end": v(-325.37, 148.74) * mm});
            skLineSegment(sketch, "E64.1", {"start": v(-325.37, 148.74) * mm, "end": v(-325.37, -32.14) * mm});
            skSolve(sketch);
        }
        {
            var Q0;
            Q0=makeQuery(id+"F14.imprint","IMPRINT",FACE,{"disambiguationData":[TD([[makeQuery(id+"F14.imprint","IMPRINT",EDGE,{"derivedFrom":sQuery(id+"F14.wireOp",EDGE,"E59.0.0")}),-1.0]])]});
            var Q1;
            {var subQ1=sQuery(id+"F14.wireOp",EDGE,"E57.0");Q1=makeQuery(id+"F14.imprint","IMPRINT",FACE,{"disambiguationData":[TD([[makeQuery(id+"F14.imprint","IMPRINT",EDGE,{"derivedFrom":subQ1}),1.0]])]});}
            var Q2;
            {var subQ1=sQuery(id+"F14.wireOp",EDGE,"E53.0");Q2=makeQuery(id+"F14.imprint","IMPRINT",FACE,{"disambiguationData":[TD([[makeQuery(id+"F14.imprint","IMPRINT",EDGE,{"derivedFrom":subQ1}),1.0]])]});}
            var Q3;
            {var subQ0=sQuery(id+"F14.wireOp",EDGE,"E52.0");var subQ3=sQuery(id+"F14.wireOp",EDGE,"E49.0");var subQ4=makeQuery(id+"F14.imprint","INTERSECT",VERTEX,{"derivedFrom":[subQ3,subQ0]});Q3=makeQuery(id+"F14.imprint","IMPRINT",FACE,{"disambiguationData":[TD([[makeQuery(id+"F14.imprint","IMPRINT",EDGE,{"disambiguationData":[TD([[subQ4,1.0]])],"derivedFrom":subQ3}),1.0]])]});}
            extrude(context, id + "F15", {"entities" : qUnion([Q0, Q1, Q2, Q3]), "depth" : 25.4 * mm});
        }
        {
            var Q0;
            Q0=makeQuery(id+"F7.opExtrude","CAP_FACE",FACE,{"disambiguationData":[OSD([sQuery(id+"F6.wireOp",EDGE,"E43.6"),sQuery(id+"F6.wireOp",EDGE,"E43.13"),sQuery(id+"F6.wireOp",EDGE,"E43.16"),sQuery(id+"F6.wireOp",EDGE,"E43.19"),sQuery(id+"F6.wireOp",EDGE,"E43.20"),sQuery(id+"F6.wireOp",EDGE,"E43.21"),sQuery(id+"F6.wireOp",EDGE,"E43.26"),sQuery(id+"F6.wireOp",EDGE,"E43.27"),sQuery(id+"F6.wireOp",EDGE,"E43.28")])],"isStart":false});
            var sketch = newSketch(context, id + "F16", { "sketchPlane" : qUnion([Q0])});
            skLineSegment(sketch, "E65.0", {"start": v(19.3, 329.8) * mm, "end": v(19.3, -32.14) * mm});
            skLineSegment(sketch, "E65.1", {"start": v(0, 329.8) * mm, "end": v(178.05, 329.8) * mm});
            skLineSegment(sketch, "E65.2", {"start": v(6.6, 329.8) * mm, "end": v(6.6, -32.14) * mm});
            skLineSegment(sketch, "E65.3", {"start": v(0, 25.4) * mm, "end": v(19.3, 25.4) * mm});
            skLineSegment(sketch, "E65.4", {"start": v(114.55, 329.8) * mm, "end": v(114.55, -32.14) * mm});
            skLineSegment(sketch, "E65.5", {"start": v(101.85, 329.8) * mm, "end": v(101.85, -32.14) * mm});
            skLineSegment(sketch, "E65.6", {"start": v(101.85, -32.14) * mm, "end": v(114.55, -32.14) * mm});
            skLineSegment(sketch, "E65.7", {"start": v(6.6, -32.14) * mm, "end": v(178.05, -32.14) * mm});
            skLineSegment(sketch, "E65.8", {"start": v(178.05, 329.8) * mm, "end": v(178.05, -32.14) * mm});
            skLineSegment(sketch, "E65.9", {"start": v(165.35, 329.8) * mm, "end": v(165.35, -32.14) * mm});
            skLineSegment(sketch, "E65.10", {"start": v(228.85, -32.14) * mm, "end": v(241.55, -32.14) * mm});
            skLineSegment(sketch, "E65.11", {"start": v(241.55, -32.14) * mm, "end": v(241.55, 283.75) * mm});
            skLineSegment(sketch, "E65.12", {"start": v(241.55, 283.75) * mm, "end": v(228.85, 283.75) * mm});
            skLineSegment(sketch, "E65.13", {"start": v(228.85, -32.14) * mm, "end": v(228.85, 283.75) * mm});
            skLineSegment(sketch, "E66.0", {"start": v(325.37, 148.74) * mm, "end": v(325.37, -32.14) * mm});
            skLineSegment(sketch, "E66.1", {"start": v(338.07, 148.74) * mm, "end": v(325.37, 148.74) * mm});
            skLineSegment(sketch, "E66.2", {"start": v(338.07, 148.74) * mm, "end": v(338.07, -32.14) * mm});
            skLineSegment(sketch, "E66.3", {"start": v(241.55, -32.14) * mm, "end": v(338.07, -32.14) * mm});
            skSolve(sketch);
        }
        {
            var Q0;
            {var subQ1=sQuery(id+"F16.wireOp",EDGE,"E65.8");Q0=makeQuery(id+"F16.imprint","IMPRINT",FACE,{"disambiguationData":[TD([[makeQuery(id+"F16.imprint","IMPRINT",EDGE,{"derivedFrom":subQ1}),-1.0]])]});}
            var Q1;
            {var subQ2=sQuery(id+"F16.wireOp",EDGE,"E65.4");Q1=makeQuery(id+"F16.imprint","IMPRINT",FACE,{"disambiguationData":[TD([[makeQuery(id+"F16.imprint","IMPRINT",EDGE,{"derivedFrom":subQ2}),-1.0]])]});}
            var Q2;
            {var subQ0=sQuery(id+"F16.wireOp",EDGE,"E65.3");var subQ3=sQuery(id+"F16.wireOp",EDGE,"E65.0");var subQ4=makeQuery(id+"F16.imprint","INTERSECT",VERTEX,{"derivedFrom":[subQ3,subQ0]});Q2=makeQuery(id+"F16.imprint","IMPRINT",FACE,{"disambiguationData":[TD([[makeQuery(id+"F16.imprint","IMPRINT",EDGE,{"disambiguationData":[TD([[subQ4,1.0]])],"derivedFrom":subQ3}),-1.0]])]});}
            extrude(context, id + "F17", {"entities" : qUnion([Q0, Q1, Q2]), "depth" : 25.4 * mm});
        }
        {
            var Q0;
            {var subQ0=sQuery(id+"F9.wireOp",EDGE,"E45.6");var subQ3=sQuery(id+"F9.wireOp",EDGE,"E45.2");var subQ4=makeQuery(id+"F9.imprint","INTERSECT",VERTEX,{"derivedFrom":[subQ3,subQ0]});Q0=makeQuery(id+"F9.imprint","IMPRINT",FACE,{"disambiguationData":[TD([[makeQuery(id+"F9.imprint","IMPRINT",EDGE,{"disambiguationData":[TD([[subQ4,-1.0]])],"derivedFrom":subQ0}),1.0]])]});}
            var Q1;
            Q1=makeQuery(id+"F9.imprint","IMPRINT",FACE,{"disambiguationData":[TD([[makeQuery(id+"F9.imprint","IMPRINT",EDGE,{"derivedFrom":sQuery(id+"F9.wireOp",EDGE,"E45.7")}),1.0]])]});
            var Q2;
            {var subQ2=sQuery(id+"F9.wireOp",EDGE,"E45.4");Q2=makeQuery(id+"F9.imprint","IMPRINT",FACE,{"disambiguationData":[TD([[makeQuery(id+"F9.imprint","IMPRINT",EDGE,{"derivedFrom":subQ2}),1.0]])]});}
            extrude(context, id + "F18", {"entities" : qUnion([Q0, Q1, Q2]), "oppositeDirection" : true, "depth" : 25.4 * mm});
        }
        {
            var Q0;
            {var subQ3=sQuery(id+"F12.wireOp",EDGE,"E47.6");var subQ5=sQuery(id+"F12.wireOp",EDGE,"E47.2");var subQ6=makeQuery(id+"F12.imprint","INTERSECT",VERTEX,{"derivedFrom":[subQ5,subQ3]});Q0=makeQuery(id+"F12.imprint","IMPRINT",FACE,{"disambiguationData":[TD([[makeQuery(id+"F12.imprint","IMPRINT",EDGE,{"disambiguationData":[TD([[subQ6,-1.0]])],"derivedFrom":subQ3}),-1.0]])]});}
            var Q1;
            Q1=makeQuery(id+"F12.imprint","IMPRINT",FACE,{"disambiguationData":[TD([[makeQuery(id+"F12.imprint","IMPRINT",EDGE,{"derivedFrom":sQuery(id+"F12.wireOp",EDGE,"E47.7")}),-1.0]])]});
            var Q2;
            {var subQ2=sQuery(id+"F12.wireOp",EDGE,"E47.4");Q2=makeQuery(id+"F12.imprint","IMPRINT",FACE,{"disambiguationData":[TD([[makeQuery(id+"F12.imprint","IMPRINT",EDGE,{"derivedFrom":subQ2}),-1.0]])]});}
            extrude(context, id + "F19", {"entities" : qUnion([Q0, Q1, Q2]), "oppositeDirection" : true, "depth" : 25.4 * mm});
        }
        {
            var Q0;
            Q0=makeQuery(id+"F14.imprint","IMPRINT",FACE,{"disambiguationData":[TD([[makeQuery(id+"F14.imprint","IMPRINT",EDGE,{"derivedFrom":sQuery(id+"F14.wireOp",EDGE,"E61.0.0")}),1.0]])]});
            var Q1;
            Q1=makeQuery(id+"F14.imprint","IMPRINT",FACE,{"disambiguationData":[TD([[makeQuery(id+"F14.imprint","IMPRINT",EDGE,{"derivedFrom":sQuery(id+"F14.wireOp",EDGE,"E60.0.0")}),1.0]])]});
            var Q2;
            {var subQ4=sQuery(id+"F14.wireOp",EDGE,"E60.0.3");Q2=makeQuery(id+"F14.imprint","IMPRINT",FACE,{"disambiguationData":[TD([[makeQuery(id+"F14.imprint","IMPRINT",EDGE,{"derivedFrom":subQ4}),1.0]])]});}
            extrude(context, id + "F20", {"entities" : qUnion([Q0, Q1, Q2]), "endBound" : BoundingType.UP_TO_NEXT, "depth" : 25.4 * mm});
        }
        {
            var Q0;
            Q0=makeQuery(id+"F1.opExtrude","CAP_FACE",FACE,{"disambiguationData":[OSD([sQuery(id+"F0.wireOp",EDGE,"E0.bottom"),sQuery(id+"F0.wireOp",EDGE,"E0.top"),sQuery(id+"F0.wireOp",EDGE,"E0.left"),sQuery(id+"F0.wireOp",EDGE,"E0.right"),sQuery(id+"F0.wireOp",EDGE,"E1.filletArc"),sQuery(id+"F0.wireOp",EDGE,"E2.filletArc"),sQuery(id+"F0.wireOp",EDGE,"E3.filletArc"),sQuery(id+"F0.wireOp",EDGE,"E4.filletArc"),sQuery(id+"F0.wireOp",EDGE,"E5"),sQuery(id+"F0.wireOp",EDGE,"E7"),sQuery(id+"F0.wireOp",EDGE,"E8"),sQuery(id+"F0.wireOp",EDGE,"E12"),sQuery(id+"F0.wireOp",EDGE,"E13"),sQuery(id+"F0.wireOp",EDGE,"E14"),sQuery(id+"F0.wireOp",EDGE,"E15"),sQuery(id+"F0.wireOp",EDGE,"E16.bottom"),sQuery(id+"F0.wireOp",EDGE,"E16.left"),sQuery(id+"F0.wireOp",EDGE,"E16.right"),sQuery(id+"F0.wireOp",EDGE,"E17.bottom"),sQuery(id+"F0.wireOp",EDGE,"E17.left"),sQuery(id+"F0.wireOp",EDGE,"E17.right"),sQuery(id+"F0.wireOp",EDGE,"E18.bottom"),sQuery(id+"F0.wireOp",EDGE,"E18.left"),sQuery(id+"F0.wireOp",EDGE,"E18.right")])],"isStart":false});
            var sketch = newSketch(context, id + "F21", { "sketchPlane" : qUnion([Q0])});
            skLineSegment(sketch, "E67.0", {"start": v(25.4, 0) * mm, "end": v(584.2, 0) * mm});
            skLineSegment(sketch, "E67.1", {"start": v(25.4, 406.4) * mm, "end": v(584.2, 406.4) * mm});
            skLineSegment(sketch, "E67.2", {"start": v(0, 25.4) * mm, "end": v(0, 381) * mm});
            skLineSegment(sketch, "E67.3", {"start": v(609.6, 25.4) * mm, "end": v(609.6, 381) * mm});
            skPoint(sketch, "E67.4", {"position": v(0, 406.4) * mm});
            skArc(sketch, "E67.5", {"start": v(25.4, 406.4) * mm, "mid": v(7.44, 398.96) * mm, "end": v(0, 381) * mm});
            skPoint(sketch, "E67.6", {"position": v(609.6, 406.4) * mm});
            skArc(sketch, "E67.7", {"start": v(609.6, 381) * mm, "mid": v(602.16, 398.96) * mm, "end": v(584.2, 406.4) * mm});
            skPoint(sketch, "E67.8", {"position": v(609.6, 0) * mm});
            skArc(sketch, "E67.9", {"start": v(584.2, 0) * mm, "mid": v(602.16, 7.44) * mm, "end": v(609.6, 25.4) * mm});
            skPoint(sketch, "E67.10", {"position": v(0, 0) * mm});
            skArc(sketch, "E67.11", {"start": v(0, 25.4) * mm, "mid": v(7.44, 7.44) * mm, "end": v(25.4, 0) * mm});
            skCircle(sketch, "E67.12", {"center": v(304.8, 355.6) * mm, "radius": 25.4 * mm});
            skLineSegment(sketch, "E67.13", {"start": v(76.2, 18.26) * mm, "end": v(113.28, 18.26) * mm});
            skLineSegment(sketch, "E67.14", {"start": v(76.2, -0.8) * mm, "end": v(76.2, 18.26) * mm});
            skLineSegment(sketch, "E67.15", {"start": v(113.28, -0.8) * mm, "end": v(113.28, 18.26) * mm});
            skCircle(sketch, "E67.16", {"center": v(83.7, 12.41) * mm, "radius": 2.15 * mm});
            skCircle(sketch, "E67.17", {"center": v(106.55, 12.41) * mm, "radius": 2.15 * mm});
            skLineSegment(sketch, "E67.18", {"start": v(76.2, -0.8) * mm, "end": v(113.28, -0.8) * mm});
            skLineSegment(sketch, "E67.19", {"start": v(286.26, 18.26) * mm, "end": v(323.34, 18.26) * mm});
            skLineSegment(sketch, "E67.20", {"start": v(286.26, -0.8) * mm, "end": v(323.34, -0.8) * mm});
            skLineSegment(sketch, "E67.21", {"start": v(286.26, 18.26) * mm, "end": v(286.26, -0.8) * mm});
            skLineSegment(sketch, "E67.22", {"start": v(323.34, 18.26) * mm, "end": v(323.34, -0.8) * mm});
            skLineSegment(sketch, "E67.23", {"start": v(496.32, 18.26) * mm, "end": v(533.4, 18.26) * mm});
            skLineSegment(sketch, "E67.24", {"start": v(496.32, -0.8) * mm, "end": v(533.4, -0.8) * mm});
            skLineSegment(sketch, "E67.25", {"start": v(496.32, 18.26) * mm, "end": v(496.32, -0.8) * mm});
            skLineSegment(sketch, "E67.26", {"start": v(533.4, 18.26) * mm, "end": v(533.4, -0.8) * mm});
            skCircle(sketch, "E67.27", {"center": v(293.75, 12.41) * mm, "radius": 2.15 * mm});
            skCircle(sketch, "E67.28", {"center": v(316.61, 12.41) * mm, "radius": 2.15 * mm});
            skCircle(sketch, "E67.29", {"center": v(503.8, 12.41) * mm, "radius": 2.15 * mm});
            skCircle(sketch, "E67.30", {"center": v(526.67, 12.41) * mm, "radius": 2.15 * mm});
            skLineSegment(sketch, "E68.0", {"start": v(94.87, 3.97) * mm, "end": v(94.87, -0.8) * mm});
            skSolve(sketch);
        }
        {
            var Q0;
            {var subQ6=sQuery(id+"F21.wireOp",EDGE,"E67.13");Q0=makeQuery(id+"F21.imprint","IMPRINT",FACE,{"disambiguationData":[TD([[makeQuery(id+"F21.imprint","IMPRINT",EDGE,{"derivedFrom":subQ6}),-1.0]])]});}
            var Q1;
            {var subQ4=sQuery(id+"F21.wireOp",EDGE,"E67.19");Q1=makeQuery(id+"F21.imprint","IMPRINT",FACE,{"disambiguationData":[TD([[makeQuery(id+"F21.imprint","IMPRINT",EDGE,{"derivedFrom":subQ4}),-1.0]])]});}
            var Q2;
            {var subQ5=sQuery(id+"F21.wireOp",EDGE,"E67.23");Q2=makeQuery(id+"F21.imprint","IMPRINT",FACE,{"disambiguationData":[TD([[makeQuery(id+"F21.imprint","IMPRINT",EDGE,{"derivedFrom":subQ5}),-1.0]])]});}
            var Q3;
            {var subQ0=sQuery(id+"F21.wireOp",EDGE,"E68.0");var subQ3=sQuery(id+"F21.wireOp",EDGE,"E67.0");var subQ4=makeQuery(id+"F21.imprint","INTERSECT",VERTEX,{"derivedFrom":[subQ3,subQ0]});Q3=makeQuery(id+"F21.imprint","IMPRINT",FACE,{"disambiguationData":[TD([[makeQuery(id+"F21.imprint","IMPRINT",EDGE,{"disambiguationData":[TD([[subQ4,-1.0]])],"derivedFrom":subQ3}),-1.0]])]});}
            extrude(context, id + "F22", {"entities" : qUnion([Q0, Q1, Q2, Q3]), "depth" : 2.03 * mm});
        }
        {
            var Q0;
            Q0=makeQuery(id+"F22.opExtrude","SWEPT_FACE",FACE,{"disambiguationData":[OSD([sQuery(id+"F21.wireOp",EDGE,"E67.15")])]});
            var sketch = newSketch(context, id + "F23", { "sketchPlane" : qUnion([Q0])});
            skCircle(sketch, "E69", {"center": v(-17.4, -0.8) * mm, "radius": 4.7 * mm});
            skSolve(sketch);
        }
        {
            var Q0;
            {var subQ0=sQuery(id+"F21.wireOp",EDGE,"E67.15");var subQ4=makeQuery(id+"F22.opExtrude","SWEPT_EDGE",EDGE,{"disambiguationData":[OSD([subQ0,sQuery(id+"F21.wireOp",EDGE,"E67.18")])]});Q0=makeQuery(id+"F23.imprint","IMPRINT",FACE,{"disambiguationData":[TD([[makeQuery(id+"F23.imprint","IMPRINT",EDGE,{"derivedFrom":subQ4}),-1.0]])]});}
            var Q1;
            {var subQ0=sQuery(id+"F21.wireOp",EDGE,"E67.15");var subQ4=makeQuery(id+"F22.opExtrude","SWEPT_EDGE",EDGE,{"disambiguationData":[OSD([subQ0,sQuery(id+"F21.wireOp",EDGE,"E67.18")])]});Q1=makeQuery(id+"F23.imprint","IMPRINT",FACE,{"disambiguationData":[TD([[makeQuery(id+"F23.imprint","IMPRINT",EDGE,{"derivedFrom":subQ4}),1.0]])]});}
            extrude(context, id + "F24", {"entities" : qUnion([Q0, Q1]), "operationType" : NewBodyOperationType.ADD, "oppositeDirection" : true, "depth" : 18.54 * mm});
        }
        {
            var Q0;
            Q0=makeQuery(id+"F22.opExtrude","SWEPT_FACE",FACE,{"disambiguationData":[OSD([sQuery(id+"F21.wireOp",EDGE,"E67.22")])]});
            var sketch = newSketch(context, id + "F25", { "sketchPlane" : qUnion([Q0])});
            skCircle(sketch, "E70.0", {"center": v(-17.4, -0.8) * mm, "radius": 4.7 * mm});
            skSolve(sketch);
        }
        {
            var Q0;
            {var subQ0=sQuery(id+"F21.wireOp",EDGE,"E67.22");var subQ1=makeQuery(id+"F22.opExtrude","CAP_EDGE",EDGE,{"disambiguationData":[OSD([subQ0])],"isStart":false});var subQ2=sQuery(id+"F25.wireOp",EDGE,"E70.0");var subQ3=makeQuery(id+"F25.imprint","INTERSECT",VERTEX,{"derivedFrom":[subQ1,subQ2]});Q0=makeQuery(id+"F25.imprint","IMPRINT",FACE,{"disambiguationData":[TD([[makeQuery(id+"F25.imprint","IMPRINT",EDGE,{"disambiguationData":[TD([[subQ3,-1.0]])],"derivedFrom":subQ2}),1.0]])]});}
            var Q1;
            Q1=sQuery(id+"F25.wireOp",EDGE,"E70.0");
            extrude(context, id + "F26", {"entities" : qUnion([Q0]), "operationType" : NewBodyOperationType.ADD, "surfaceEntities" : qUnion([Q1]), "oppositeDirection" : true, "depth" : 18.54 * mm});
        }
        {
            var Q0;
            Q0=makeQuery(id+"F22.opExtrude","SWEPT_FACE",FACE,{"disambiguationData":[OSD([sQuery(id+"F21.wireOp",EDGE,"E67.26")])]});
            var sketch = newSketch(context, id + "F27", { "sketchPlane" : qUnion([Q0])});
            skCircle(sketch, "E71.0", {"center": v(-17.4, -0.8) * mm, "radius": 4.7 * mm});
            skSolve(sketch);
        }
        {
            var Q0;
            {var subQ0=sQuery(id+"F21.wireOp",EDGE,"E67.26");var subQ1=makeQuery(id+"F22.opExtrude","CAP_EDGE",EDGE,{"disambiguationData":[OSD([subQ0])],"isStart":false});var subQ2=sQuery(id+"F27.wireOp",EDGE,"E71.0");var subQ3=makeQuery(id+"F27.imprint","INTERSECT",VERTEX,{"derivedFrom":[subQ1,subQ2]});Q0=makeQuery(id+"F27.imprint","IMPRINT",FACE,{"disambiguationData":[TD([[makeQuery(id+"F27.imprint","IMPRINT",EDGE,{"disambiguationData":[TD([[subQ3,-1.0]])],"derivedFrom":subQ2}),1.0]])]});}
            extrude(context, id + "F28", {"entities" : qUnion([Q0]), "operationType" : NewBodyOperationType.ADD, "oppositeDirection" : true, "depth" : 18.54 * mm});
        }
        {
            var Q0;
            Q0=makeQuery(id+"F14.imprint","IMPRINT",FACE,{"disambiguationData":[TD([[makeQuery(id+"F14.imprint","IMPRINT",EDGE,{"derivedFrom":sQuery(id+"F14.wireOp",EDGE,"E59.0.1")}),-1.0]])]});
            extrude(context, id + "F29", {"entities" : qUnion([Q0]), "endBound" : BoundingType.UP_TO_NEXT, "depth" : 25.4 * mm});
        }
        {
            var Q0;
            {var subQ4=sQuery(id+"F14.wireOp",EDGE,"E64.0");Q0=makeQuery(id+"F14.imprint","IMPRINT",FACE,{"disambiguationData":[TD([[makeQuery(id+"F14.imprint","IMPRINT",EDGE,{"derivedFrom":subQ4}),-1.0]])]});}
            extrude(context, id + "F30", {"entities" : qUnion([Q0]), "endBound" : BoundingType.UP_TO_NEXT, "depth" : 25.4 * mm});
        }
        {
            var Q0;
            Q0=makeQuery(id+"F4.opExtrude","CAP_FACE",FACE,{"disambiguationData":[OSD([sQuery(id+"F3.wireOp",EDGE,"E22"),sQuery(id+"F3.wireOp",EDGE,"E25.top"),sQuery(id+"F3.wireOp",EDGE,"E26"),sQuery(id+"F3.wireOp",EDGE,"E29"),sQuery(id+"F3.wireOp",EDGE,"E30"),sQuery(id+"F3.wireOp",EDGE,"E31"),sQuery(id+"F3.wireOp",EDGE,"E36"),sQuery(id+"F3.wireOp",EDGE,"E37"),sQuery(id+"F3.wireOp",EDGE,"E38"),sQuery(id+"F3.wireOp",EDGE,"E42.left")])],"isStart":true});
            var sketch = newSketch(context, id + "F31", { "sketchPlane" : qUnion([Q0])});
            skCircle(sketch, "E72", {"center": v(32, 342.9) * mm, "radius": 12.7 * mm});
            skCircle(sketch, "E73", {"center": v(32, 63.5) * mm, "radius": 12.7 * mm});
            skSolve(sketch);
        }
        {
            var Q0;
            {Q0=qUnion([makeQuery(id+"F31.imprint","IMPRINT",FACE,{"disambiguationData":[TD([[makeQuery(id+"F31.imprint","IMPRINT",EDGE,{"derivedFrom":sQuery(id+"F31.wireOp",EDGE,"E72")}),1.0]])]}),makeQuery(id+"F31.imprint","IMPRINT",FACE,{"disambiguationData":[TD([[makeQuery(id+"F31.imprint","IMPRINT",EDGE,{"derivedFrom":sQuery(id+"F31.wireOp",EDGE,"E73")}),1.0]])]})]);}
            extrude(context, id + "F32", {"entities" : qUnion([Q0]), "operationType" : NewBodyOperationType.REMOVE, "endBound" : BoundingType.THROUGH_ALL, "oppositeDirection" : true, "depth" : 25.4 * mm});
        }
        {
            var Q0;
            Q0=makeQuery(id+"F31.imprint","IMPRINT",FACE,{"disambiguationData":[TD([[makeQuery(id+"F31.imprint","IMPRINT",EDGE,{"derivedFrom":sQuery(id+"F31.wireOp",EDGE,"E72")}),-1.0]])]});
            var sketch = newSketch(context, id + "F33", { "sketchPlane" : qUnion([Q0])});
            skCircle(sketch, "E74", {"center": v(32, 304.4) * mm, "radius": 12.7 * mm});
            skSolve(sketch);
        }
        {
            var Q0;
            Q0=makeQuery(id+"F33.imprint","IMPRINT",FACE,{"disambiguationData":[TD([[makeQuery(id+"F33.imprint","IMPRINT",EDGE,{"derivedFrom":sQuery(id+"F33.wireOp",EDGE,"E74")}),1.0]])]});
            extrude(context, id + "F34", {"entities" : qUnion([Q0]), "operationType" : NewBodyOperationType.REMOVE, "endBound" : BoundingType.THROUGH_ALL, "oppositeDirection" : true, "depth" : 25.4 * mm});
        }
        {
            var Q0;
            Q0=makeQuery(id+"F21.imprint","IMPRINT",FACE,{"disambiguationData":[TD([[makeQuery(id+"F21.imprint","IMPRINT",EDGE,{"derivedFrom":sQuery(id+"F21.wireOp",EDGE,"E67.1")}),-1.0]])]});
            var sketch = newSketch(context, id + "F35", { "sketchPlane" : qUnion([Q0])});
            skLineSegment(sketch, "E75.0", {"start": v(19.05, -44.84) * mm, "end": v(19.05, 148.74) * mm});
            skLineSegment(sketch, "E75.1", {"start": v(31.75, -32.14) * mm, "end": v(31.75, 283.75) * mm});
            skLineSegment(sketch, "E75.2", {"start": v(266.7, 25.4) * mm, "end": v(266.7, -32.14) * mm});
            skLineSegment(sketch, "E75.3", {"start": v(279.4, 25.4) * mm, "end": v(279.4, -32.14) * mm});
            skLineSegment(sketch, "E75.4", {"start": v(330.2, 25.4) * mm, "end": v(330.2, -32.14) * mm});
            skLineSegment(sketch, "E75.5", {"start": v(342.9, 25.4) * mm, "end": v(342.9, -32.14) * mm});
            skLineSegment(sketch, "E75.6", {"start": v(577.85, 329.8) * mm, "end": v(577.85, -32.14) * mm});
            skLineSegment(sketch, "E75.7", {"start": v(590.55, 25.4) * mm, "end": v(590.55, -44.84) * mm});
            skLineSegment(sketch, "E76.0", {"start": v(25.4, 0) * mm, "end": v(584.2, 0) * mm});
            skLineSegment(sketch, "E76.1", {"start": v(25.4, 406.4) * mm, "end": v(584.2, 406.4) * mm});
            skCircle(sketch, "E77", {"center": v(25.4, 342.9) * mm, "radius": 2.15 * mm});
            skCircle(sketch, "E78", {"center": v(273.05, 304.4) * mm, "radius": 2.15 * mm});
            skCircle(sketch, "E79", {"center": v(336.55, 304.4) * mm, "radius": 2.15 * mm});
            skCircle(sketch, "E80", {"center": v(25.4, 63.5) * mm, "radius": 2.15 * mm});
            skCircle(sketch, "E81", {"center": v(273.05, 63.5) * mm, "radius": 2.15 * mm});
            skCircle(sketch, "E82", {"center": v(336.55, 63.5) * mm, "radius": 2.15 * mm});
            skCircle(sketch, "E83", {"center": v(584.2, 342.9) * mm, "radius": 2.15 * mm});
            skCircle(sketch, "E84", {"center": v(584.2, 63.5) * mm, "radius": 2.15 * mm});
            skSolve(sketch);
        }
        {
            var Q0;
            Q0=makeQuery(id+"F35.imprint","IMPRINT",FACE,{"disambiguationData":[TD([[makeQuery(id+"F35.imprint","IMPRINT",EDGE,{"derivedFrom":sQuery(id+"F35.wireOp",EDGE,"E77")}),1.0]])]});
            var Q1;
            Q1=makeQuery(id+"F35.imprint","IMPRINT",FACE,{"disambiguationData":[TD([[makeQuery(id+"F35.imprint","IMPRINT",EDGE,{"derivedFrom":sQuery(id+"F35.wireOp",EDGE,"E78")}),1.0]])]});
            var Q2;
            Q2=makeQuery(id+"F35.imprint","IMPRINT",FACE,{"disambiguationData":[TD([[makeQuery(id+"F35.imprint","IMPRINT",EDGE,{"derivedFrom":sQuery(id+"F35.wireOp",EDGE,"E79")}),1.0]])]});
            var Q3;
            Q3=makeQuery(id+"F35.imprint","IMPRINT",FACE,{"disambiguationData":[TD([[makeQuery(id+"F35.imprint","IMPRINT",EDGE,{"derivedFrom":sQuery(id+"F35.wireOp",EDGE,"E83")}),1.0]])]});
            var Q4;
            Q4=makeQuery(id+"F35.imprint","IMPRINT",FACE,{"disambiguationData":[TD([[makeQuery(id+"F35.imprint","IMPRINT",EDGE,{"derivedFrom":sQuery(id+"F35.wireOp",EDGE,"E84")}),1.0]])]});
            var Q5;
            Q5=makeQuery(id+"F35.imprint","IMPRINT",FACE,{"disambiguationData":[TD([[makeQuery(id+"F35.imprint","IMPRINT",EDGE,{"derivedFrom":sQuery(id+"F35.wireOp",EDGE,"E82")}),1.0]])]});
            var Q6;
            Q6=makeQuery(id+"F35.imprint","IMPRINT",FACE,{"disambiguationData":[TD([[makeQuery(id+"F35.imprint","IMPRINT",EDGE,{"derivedFrom":sQuery(id+"F35.wireOp",EDGE,"E81")}),1.0]])]});
            var Q7;
            Q7=makeQuery(id+"F35.imprint","IMPRINT",FACE,{"disambiguationData":[TD([[makeQuery(id+"F35.imprint","IMPRINT",EDGE,{"derivedFrom":sQuery(id+"F35.wireOp",EDGE,"E80")}),1.0]])]});
            extrude(context, id + "F36", {"entities" : qUnion([Q0, Q1, Q2, Q3, Q4, Q5, Q6, Q7]), "operationType" : NewBodyOperationType.REMOVE, "oppositeDirection" : true, "depth" : 50.8 * mm});
        }
    });
